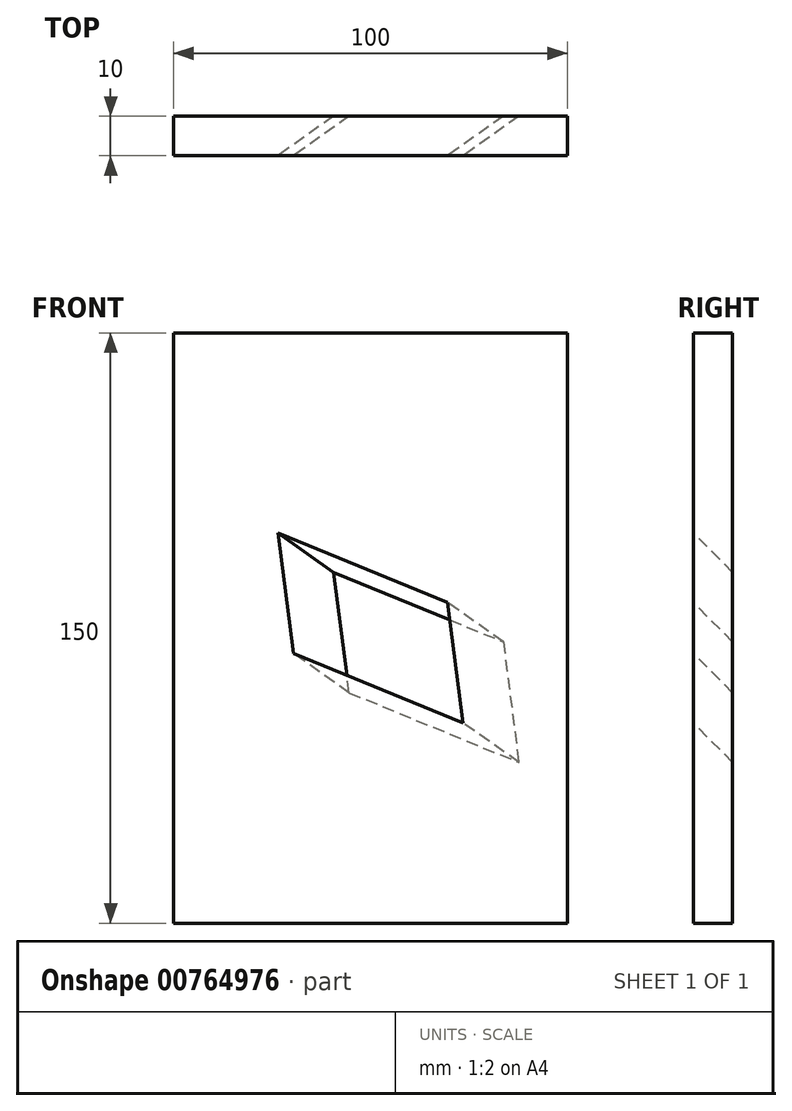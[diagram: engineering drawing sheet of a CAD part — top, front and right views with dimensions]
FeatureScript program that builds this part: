
annotation { "Feature Type Name" : "Feature", "Feature Type Description" : "" }
export const myFeature = defineFeature(function(context is Context, id is Id, definition is map)
    precondition{}
    {
        {
            var Q0;
            Q0=qCreatedBy(makeId("Front.planeOp"),FACE);
            var sketch = newSketch(context, id + "F0", { "sketchPlane" : qUnion([Q0])});
            skLineSegment(sketch, "E0.bottom", {"start": v(50, -75) * mm, "end": v(-50, -75) * mm});
            skLineSegment(sketch, "E0.top", {"start": v(50, 75) * mm, "end": v(-50, 75) * mm});
            skLineSegment(sketch, "E0.left", {"start": v(50, -75) * mm, "end": v(50, 75) * mm});
            skLineSegment(sketch, "E0.right", {"start": v(-50, -75) * mm, "end": v(-50, 75) * mm});
            skPoint(sketch, "E0.middle", {"position": v(0, 0) * mm});
            skSolve(sketch);
        }
        {
            var Q0;
            Q0 = qSketchRegion(id + "F0", true);
            extrude(context, id + "F1", {"entities" : qUnion([Q0]), "oppositeDirection" : true, "depth" : 10 * mm, "offsetDistance" : 25 * mm});
        }
        {
            var Q0;
            Q0=qCreatedBy(makeId("Right.planeOp"),FACE);
            var sketch = newSketch(context, id + "F2", { "sketchPlane" : qUnion([Q0])});
            skLineSegment(sketch, "E1", {"start": v(0, 0) * mm, "end": v(-70.71, 70.71) * mm});
            skSolve(sketch);
        }
        {
            var Q0;
            Q0=sQuery(id+"F2.wireOp",EDGE,"E1");
            cPlane(context, id + "F3", {"entities" : qUnion([Q0]), "cplaneType" : CPlaneType.LINE_ANGLE, "offset" : 25 * mm, "angle" : 0 * degree, "width" : 150 * mm, "height" : 150 * mm});
        }
        {
            var Q0;
            Q0=qCreatedBy(id+"F3.planeOp",FACE);
            var sketch = newSketch(context, id + "F4", { "sketchPlane" : qUnion([Q0])});
            skLineSegment(sketch, "E2", {"start": v(0, 0) * mm, "end": v(-70.71, 70.71) * mm});
            skSolve(sketch);
        }
        {
            var Q0;
            Q0=sQuery(id+"F4.wireOp",VERTEX,"E2.end");
            var Q1;
            Q1=sQuery(id+"F4.wireOp",EDGE,"E2");
            cPlane(context, id + "F5", {"entities" : qUnion([Q0, Q1]), "cplaneType" : CPlaneType.LINE_POINT, "offset" : 25 * mm, "width" : 150 * mm, "height" : 150 * mm});
        }
        {
            var Q0;
            Q0=qCreatedBy(id+"F5.planeOp",FACE);
            var sketch = newSketch(context, id + "F6", { "sketchPlane" : qUnion([Q0])});
            skLineSegment(sketch, "E3", {"start": v(0, 0) * mm, "end": v(5.23, -11.35) * mm, "construction": true});
            skLineSegment(sketch, "E4", {"start": v(-6.12, -16.58) * mm, "end": v(16.58, -6.12) * mm});
            skLineSegment(sketch, "E5", {"start": v(-6.12, -16.58) * mm, "end": v(-16.58, 6.12) * mm});
            skLineSegment(sketch, "E6", {"start": v(-16.58, 6.12) * mm, "end": v(6.12, 16.58) * mm});
            skLineSegment(sketch, "E7", {"start": v(6.12, 16.58) * mm, "end": v(16.58, -6.12) * mm});
            skLineSegment(sketch, "E8", {"start": v(-11.35, -5.23) * mm, "end": v(11.35, 5.23) * mm, "construction": true});
            skLineSegment(sketch, "E9", {"start": v(0, 0) * mm, "end": v(66.55, -47.06) * mm, "construction": true});
            skSolve(sketch);
        }
        {
            var Q0;
            Q0 = qSketchRegion(id + "F6", true);
            extrude(context, id + "F7", {"entities" : qUnion([Q0]), "operationType" : NewBodyOperationType.REMOVE, "endBound" : BoundingType.THROUGH_ALL, "oppositeDirection" : true, "depth" : 25 * mm, "offsetDistance" : 25 * mm});
        }
    });
